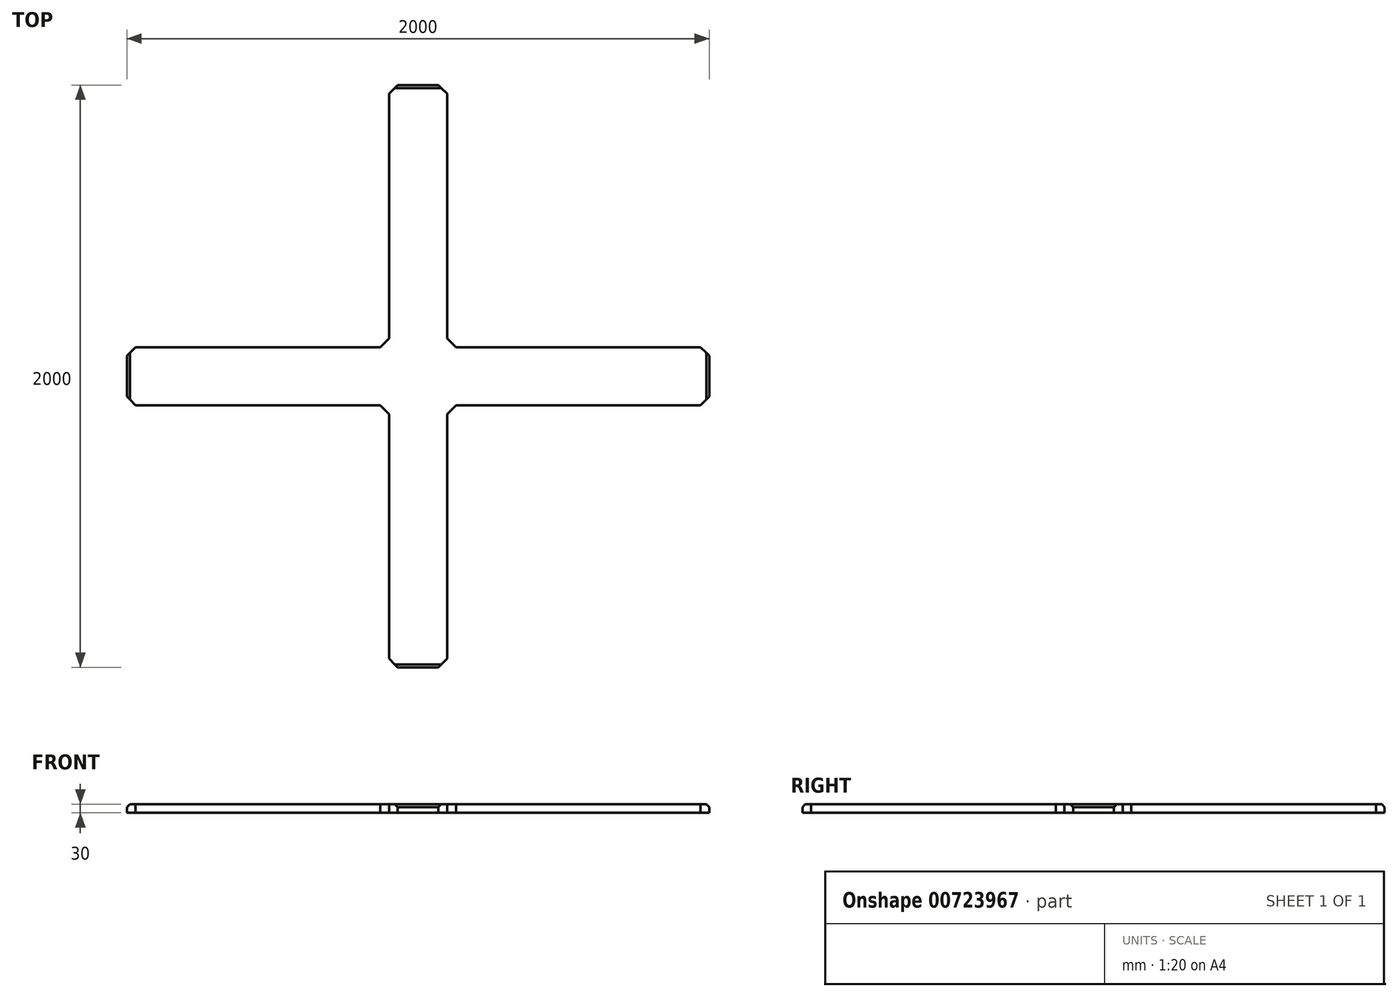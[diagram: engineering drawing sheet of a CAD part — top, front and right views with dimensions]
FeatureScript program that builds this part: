
annotation { "Feature Type Name" : "Feature", "Feature Type Description" : "" }
export const myFeature = defineFeature(function(context is Context, id is Id, definition is map)
    precondition{}
    {
        {
            var Q0;
            Q0=qCreatedBy(makeId("Top.planeOp"),FACE);
            var sketch = newSketch(context, id + "F0", { "sketchPlane" : qUnion([Q0])});
            skPoint(sketch, "E0.startSnap0", {"position": v(-893.79, 347.86) * mm});
            skLineSegment(sketch, "E1", {"start": v(-1993.79, 747.86) * mm, "end": v(6.21, 747.86) * mm});
            skLineSegment(sketch, "E2", {"start": v(-1993.79, 547.86) * mm, "end": v(6.21, 547.86) * mm});
            skLineSegment(sketch, "E3", {"start": v(-893.79, 1647.86) * mm, "end": v(-893.79, -352.14) * mm});
            skLineSegment(sketch, "E4", {"start": v(-1093.79, 1647.86) * mm, "end": v(-1093.79, -352.14) * mm});
            skLineSegment(sketch, "E5", {"start": v(-1093.79, 1647.86) * mm, "end": v(-893.79, 1647.86) * mm});
            skLineSegment(sketch, "E6", {"start": v(6.21, 747.86) * mm, "end": v(6.21, 547.86) * mm});
            skLineSegment(sketch, "E7", {"start": v(-893.79, -352.14) * mm, "end": v(-1093.79, -352.14) * mm});
            skLineSegment(sketch, "E8", {"start": v(-1993.79, 547.86) * mm, "end": v(-1993.79, 747.86) * mm});
            skSolve(sketch);
        }
        {
            var Q0;
            Q0 = qSketchRegion(id + "F0", true);
            extrude(context, id + "F1", {"entities" : qUnion([Q0]), "depth" : 30 * mm, "offsetDistance" : 25 * mm});
        }
        {
            var Q0;
            Q0=makeQuery(id+"F1.opExtrude","SWEPT_EDGE",EDGE,{"disambiguationData":[OSD([sQuery(id+"F0.wireOp",EDGE,"E2"),sQuery(id+"F0.wireOp",EDGE,"TrDkYI6D-UIGH-nejy-xpNl-u3Bwt3jzgq7e")])]});
            var Q1;
            Q1=makeQuery(id+"F1.opExtrude","SWEPT_EDGE",EDGE,{"disambiguationData":[OSD([sQuery(id+"F0.wireOp",EDGE,"E3"),sQuery(id+"F0.wireOp",EDGE,"18j6OHr4-TRrr-pv8Y-Eycb-Oa9IyfdOlugE")])]});
            var Q2;
            Q2=makeQuery(id+"F1.opExtrude","SWEPT_EDGE",EDGE,{"disambiguationData":[OSD([sQuery(id+"F0.wireOp",EDGE,"E4"),sQuery(id+"F0.wireOp",EDGE,"18j6OHr4-TRrr-pv8Y-Eycb-Oa9IyfdOlugE")])]});
            var Q3;
            Q3=makeQuery(id+"F1.opExtrude","SWEPT_EDGE",EDGE,{"disambiguationData":[OSD([sQuery(id+"F0.wireOp",EDGE,"E1"),sQuery(id+"F0.wireOp",EDGE,"TrDkYI6D-UIGH-nejy-xpNl-u3Bwt3jzgq7e")])]});
            var Q4;
            Q4=makeQuery(id+"F1.opExtrude","SWEPT_EDGE",EDGE,{"disambiguationData":[OSD([sQuery(id+"F0.wireOp",EDGE,"E3"),sQuery(id+"F0.wireOp",EDGE,"YtTpaHuj-CRqu-kIpA-fmCY-DyEtPChT2qtX")])]});
            var Q5;
            Q5=makeQuery(id+"F1.opExtrude","SWEPT_EDGE",EDGE,{"disambiguationData":[OSD([sQuery(id+"F0.wireOp",EDGE,"E2"),sQuery(id+"F0.wireOp",EDGE,"XOWuIDGt-CBr5-vbnb-ZTu6-pa1dFoiLWOnU")])]});
            var Q6;
            Q6=makeQuery(id+"F1.opExtrude","SWEPT_EDGE",EDGE,{"disambiguationData":[OSD([sQuery(id+"F0.wireOp",EDGE,"E1"),sQuery(id+"F0.wireOp",EDGE,"XOWuIDGt-CBr5-vbnb-ZTu6-pa1dFoiLWOnU")])]});
            var Q7;
            Q7=makeQuery(id+"F1.opExtrude","SWEPT_EDGE",EDGE,{"disambiguationData":[OSD([sQuery(id+"F0.wireOp",EDGE,"E4"),sQuery(id+"F0.wireOp",EDGE,"YtTpaHuj-CRqu-kIpA-fmCY-DyEtPChT2qtX")])]});
            chamfer(context, id + "F2", {"entities" : qUnion([Q0, Q1, Q2, Q3, Q4, Q5, Q6, Q7]), "width" : 30 * mm, "tangentPropagation" : true});
        }
        {
            var Q0;
            Q0=makeQuery(id+"F1.opExtrude","CAP_EDGE",EDGE,{"disambiguationData":[OSD([sQuery(id+"F0.wireOp",EDGE,"E7")])],"isStart":false});
            var Q1;
            Q1=makeQuery(id+"F1.opExtrude","CAP_EDGE",EDGE,{"disambiguationData":[OSD([sQuery(id+"F0.wireOp",EDGE,"E6")])],"isStart":false});
            var Q2;
            Q2=makeQuery(id+"F1.opExtrude","CAP_EDGE",EDGE,{"disambiguationData":[OSD([sQuery(id+"F0.wireOp",EDGE,"E5")])],"isStart":false});
            var Q3;
            Q3=makeQuery(id+"F1.opExtrude","CAP_EDGE",EDGE,{"disambiguationData":[OSD([sQuery(id+"F0.wireOp",EDGE,"E8")])],"isStart":false});
            chamfer(context, id + "F3", {"entities" : qUnion([Q0, Q1, Q2, Q3]), "width" : 10 * mm, "tangentPropagation" : true});
        }
    });
